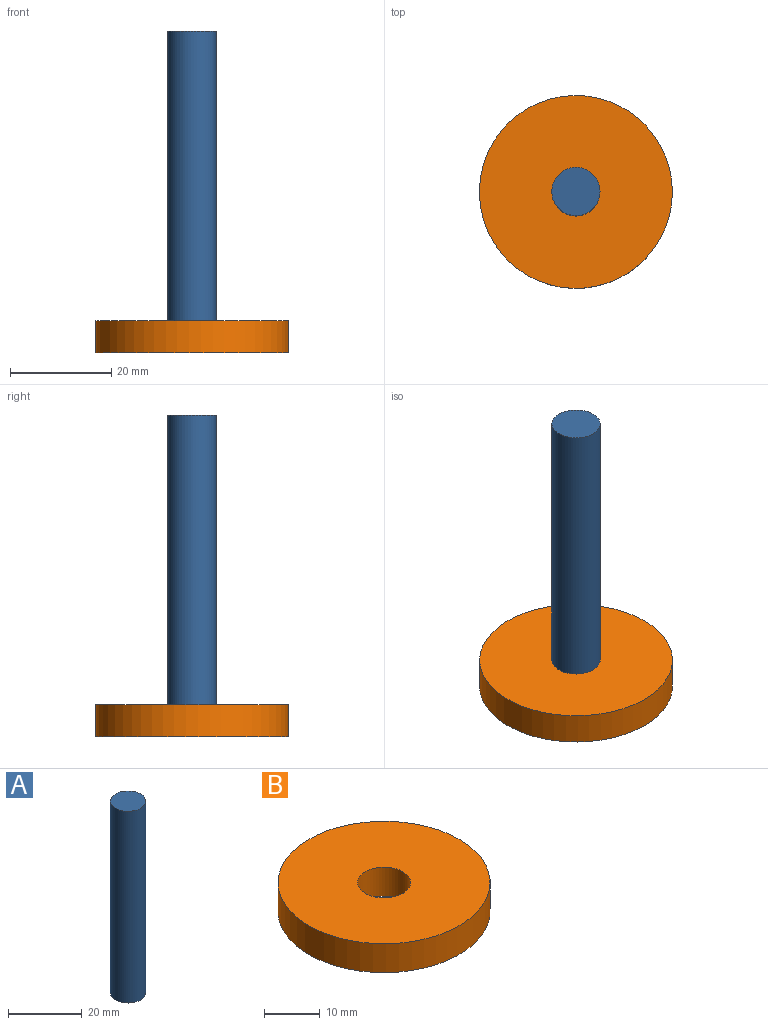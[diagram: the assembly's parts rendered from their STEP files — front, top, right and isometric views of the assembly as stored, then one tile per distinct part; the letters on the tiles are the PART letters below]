
ASSEMBLY  parts=2 mates=1
PART A: 3 faces, bbox 9.5x9.5x63.5 mm
  f0: plane 9.53x9.53mm, normal (0,0,1), area 71.3mm2, adj f1
  f1: cylinder r=4.76mm len=63.5mm, axis (0,0,-1), area 1900.2mm2, adj f0,f2
  f2: plane 9.53x9.53mm, normal (0,0,-1), area 71.3mm2, adj f1
PART B: 4 faces, bbox 38.1x38.1x6.4 mm
  f0: cylinder r=4.76mm len=9.53mm, axis (0,0,-1), area 190mm2, adj f2,f3
  f1: cylinder r=19.05mm len=38.1mm, axis (0,0,-1), area 760.1mm2, adj f2,f3
  f2: plane 38.1x38.1mm, normal (0,0,1), area 1068.8mm2, adj f0,f1
  f3: plane 38.1x38.1mm, normal (0,0,-1), area 1068.8mm2, adj f0,f1
PLACE A t=(-31.75,0,-76.2)mm
PLACE B t=(-31.75,0,-76.2)mm
MATE fastened A.f1 <-> B.f1  axis (0,0,-1) through (0,0,-6.35)mm
